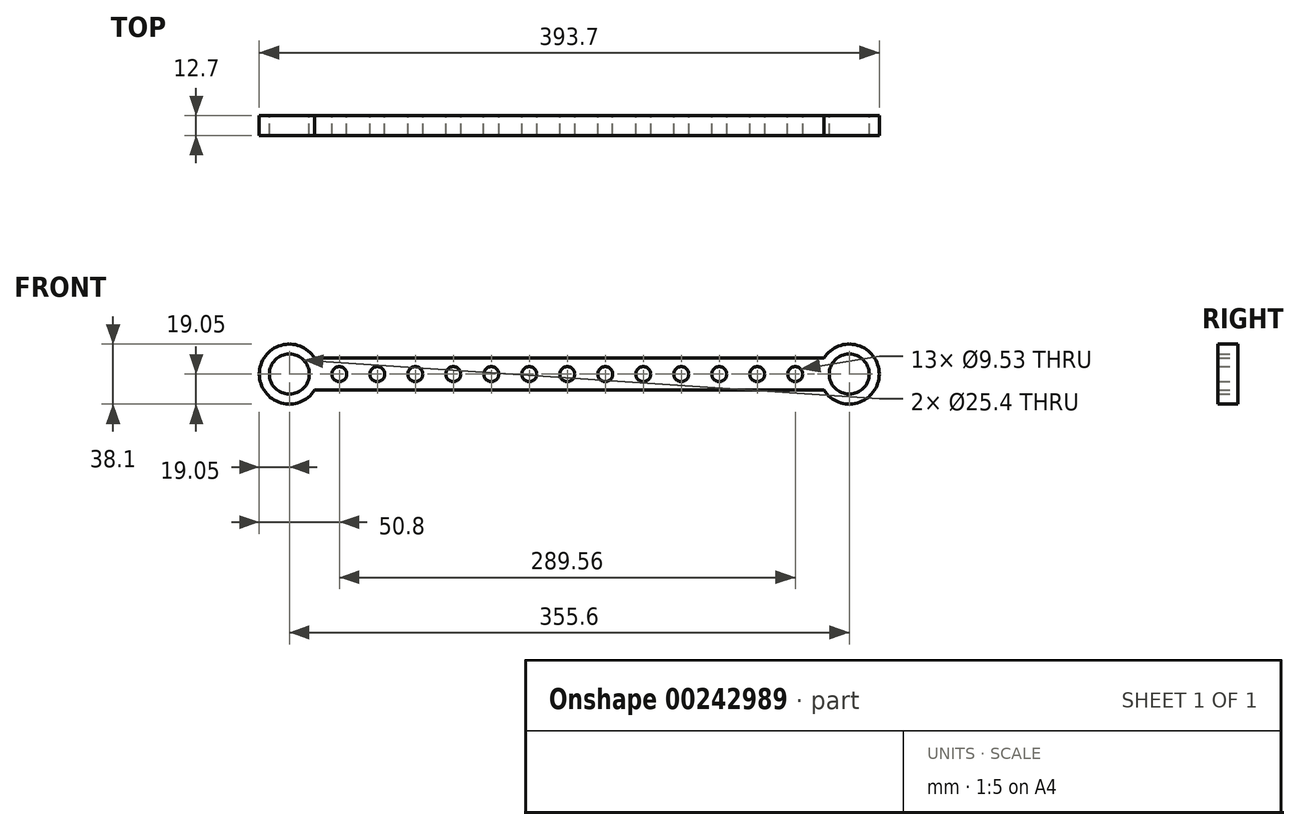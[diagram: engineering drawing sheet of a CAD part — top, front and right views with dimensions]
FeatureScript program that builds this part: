
annotation { "Feature Type Name" : "Feature", "Feature Type Description" : "" }
export const myFeature = defineFeature(function(context is Context, id is Id, definition is map)
    precondition{}
    {
        {
            var Q0;
            Q0=qCreatedBy(makeId("Front.planeOp"),FACE);
            var sketch = newSketch(context, id + "F0", { "sketchPlane" : qUnion([Q0])});
            skArc(sketch, "E0", {"start": v(-16.11, -10.16) * mm, "mid": v(19.05, 0) * mm, "end": v(-16.11, 10.16) * mm});
            skArc(sketch, "E1", {"start": v(-339.49, 10.16) * mm, "mid": v(-374.65, 0) * mm, "end": v(-339.49, -10.16) * mm});
            skLineSegment(sketch, "E2", {"start": v(-339.49, 10.16) * mm, "end": v(-16.11, 10.16) * mm});
            skLineSegment(sketch, "E3", {"start": v(-336.55, 0) * mm, "end": v(-19.05, 0) * mm, "construction": true});
            skLineSegment(sketch, "E4.MirrorCS", {"start": v(-339.49, -10.16) * mm, "end": v(-16.11, -10.16) * mm});
            skCircle(sketch, "E5", {"center": v(-355.6, 0) * mm, "radius": 12.7 * mm});
            skCircle(sketch, "E6", {"center": v(0, 0) * mm, "radius": 12.7 * mm});
            skPoint(sketch, "E7", {"position": v(-323.85, 0) * mm});
            skPoint(sketch, "E8.1.0.0", {"position": v(-299.72, 0) * mm});
            skPoint(sketch, "E8.2.0.0", {"position": v(-275.59, 0) * mm});
            skPoint(sketch, "E8.3.0.0", {"position": v(-251.46, 0) * mm});
            skPoint(sketch, "E8.4.0.0", {"position": v(-227.33, 0) * mm});
            skPoint(sketch, "E8.5.0.0", {"position": v(-203.2, 0) * mm});
            skPoint(sketch, "E8.6.0.0", {"position": v(-179.07, 0) * mm});
            skPoint(sketch, "E8.7.0.0", {"position": v(-154.94, 0) * mm});
            skPoint(sketch, "E8.8.0.0", {"position": v(-130.8, 0) * mm});
            skPoint(sketch, "E8.9.0.0", {"position": v(-106.68, 0) * mm});
            skLineSegment(sketch, "E8.direction1", {"start": v(-323.85, 0) * mm, "end": v(-299.72, 0) * mm, "construction": true});
            skPoint(sketch, "E9.0.10.0", {"position": v(-82.55, 0) * mm});
            skPoint(sketch, "E10.0.11.0", {"position": v(-58.42, 0) * mm});
            skPoint(sketch, "E11.0.12.0", {"position": v(-34.29, 0) * mm});
            skSolve(sketch);
        }
        {
            var Q0;
            Q0 = qSketchRegion(id + "F0", true);
            extrude(context, id + "F1", {"entities" : qUnion([Q0]), "depth" : 12.7 * mm});
        }
        {
            var Q0;
            Q0=sQuery(id+"F0.wireOp",VERTEX,"E7");
            var Q1;
            Q1=sQuery(id+"F0.wireOp",VERTEX,"E8.1.0.0");
            var Q2;
            Q2=sQuery(id+"F0.wireOp",VERTEX,"E8.2.0.0");
            var Q3;
            Q3=sQuery(id+"F0.wireOp",VERTEX,"E8.3.0.0");
            var Q4;
            Q4=sQuery(id+"F0.wireOp",VERTEX,"E8.4.0.0");
            var Q5;
            Q5=sQuery(id+"F0.wireOp",VERTEX,"E8.5.0.0");
            var Q6;
            Q6=sQuery(id+"F0.wireOp",VERTEX,"E8.6.0.0");
            var Q7;
            Q7=sQuery(id+"F0.wireOp",VERTEX,"E8.7.0.0");
            var Q8;
            Q8=sQuery(id+"F0.wireOp",VERTEX,"E8.8.0.0");
            var Q9;
            Q9=sQuery(id+"F0.wireOp",VERTEX,"E8.9.0.0");
            var Q10;
            Q10=sQuery(id+"F0.wireOp",VERTEX,"E9.0.10.0");
            var Q11;
            Q11=sQuery(id+"F0.wireOp",VERTEX,"E10.0.11.0");
            var Q12;
            Q12=sQuery(id+"F0.wireOp",VERTEX,"E11.0.12.0");
            var Q13;
            Q13=makeQuery(id+"F1.opExtrude","SWEPT_BODY",BODY,{"disambiguationData":[OSD([sQuery(id+"F0.wireOp",EDGE,"E0"),sQuery(id+"F0.wireOp",EDGE,"E1"),sQuery(id+"F0.wireOp",EDGE,"E2"),sQuery(id+"F0.wireOp",EDGE,"E4.MirrorCS"),sQuery(id+"F0.wireOp",EDGE,"E5"),sQuery(id+"F0.wireOp",EDGE,"E6")])]});
            hole(context, id + "F2", {"style" : HoleStyle.SIMPLE, "endStyle" : HoleEndStyle.THROUGH, "oppositeDirection" : true, "holeDiameter" : 9.52 * mm, "tappedDepth" : 12.7 * mm, "tapClearance" : 3, "startFromSketch" : true, "locations" : qUnion([Q0, Q1, Q2, Q3, Q4, Q5, Q6, Q7, Q8, Q9, Q10, Q11, Q12]), "scope" : qUnion([Q13])});
        }
    });
